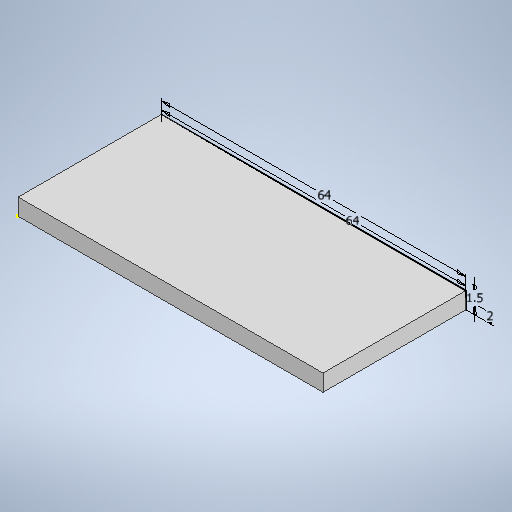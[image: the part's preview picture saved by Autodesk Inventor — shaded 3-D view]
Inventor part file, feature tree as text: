
AUTODESK INVENTOR PART (.ipt)
format: ipt  version: 2025.1 (Build 291241020, 241B)  size: 229,888 bytes
history: native  units: mm
features: sketch x3, extrude x2
ambient origin geometry x8: Origin, YZ Plane, XZ Plane, XY Plane, X Axis, Y Axis, Z Axis, Center Point
bodies: Solid1 (feature_tree)
feature tree (5):
  sketch  "Sketch1"  dims[d0=64.0mm d1=2.0mm]
  extrude  "Extrusion1"  Depth=2.0mm
  sketch  "Sketch2"  dims[d2=30.0mm d3=0.0mm d4=64.0mm]
  sketch  "Sketch3"  dims[d5=1.5mm d6=30.0mm d7=0.0mm]
  extrude  "Extrusion2"  Depth=64.0mm
